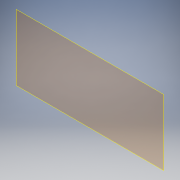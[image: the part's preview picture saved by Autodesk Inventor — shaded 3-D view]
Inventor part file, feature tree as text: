
AUTODESK INVENTOR PART (.ipt)
format: ipt  version: 2019 (Build 230136000, 136)  size: 82,432 bytes
history: native  units: mm
features: other x3, plane x1
ambient origin geometry x8: Origin, YZ Plane, XZ Plane, XY Plane, X Axis, Y Axis, Z Axis, Center Point
feature tree (4):
  plane  "Arbeitsebene1"
  other  "<userpath>\Google Drive\Projekte\makroboard\makroboard_case\Baugruppe1.iam"
  other  "Baugruppe1.iam"
  other  "makroboard:1"
